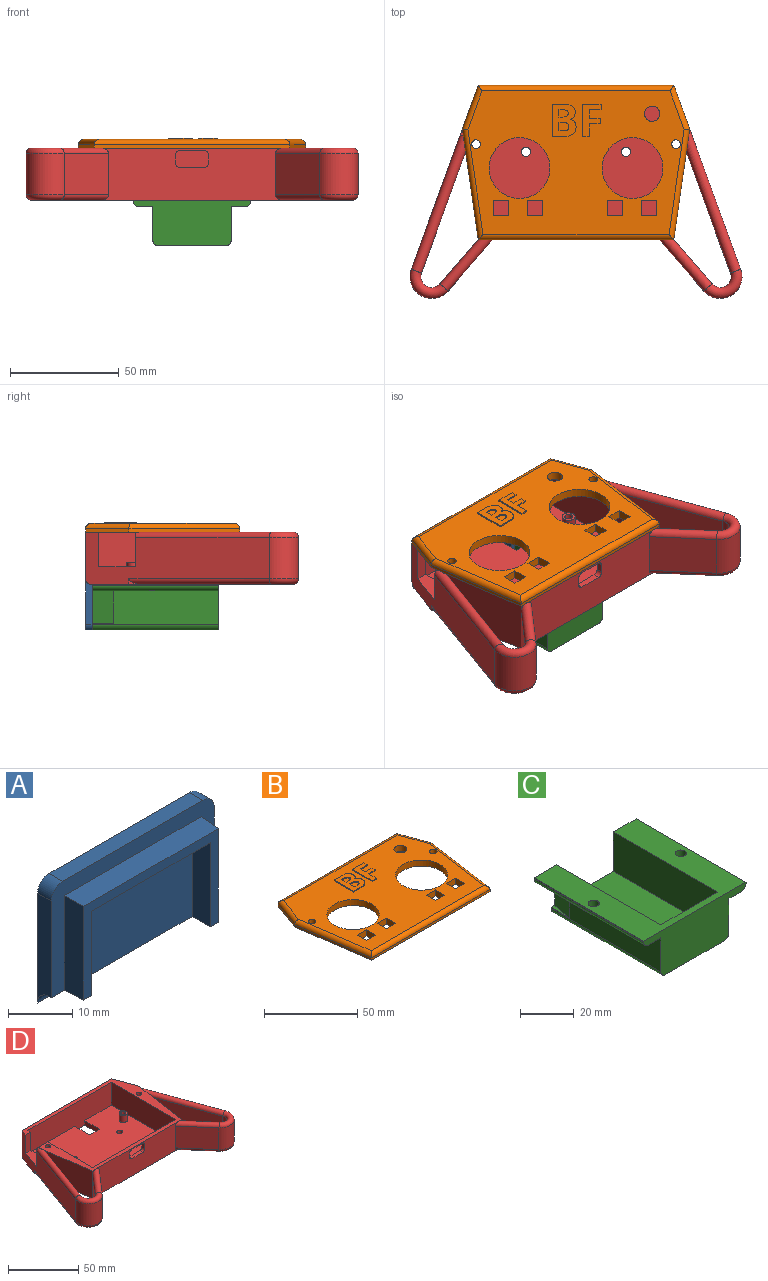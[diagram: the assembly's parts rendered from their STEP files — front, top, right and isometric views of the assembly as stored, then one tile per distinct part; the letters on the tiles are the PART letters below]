
ASSEMBLY  parts=4 mates=7
PART A: 17 faces, bbox 36x7x23.5 mm
  f0: plane 36x21mm, normal (0,-1,0), area 206.7mm2, adj f1,f2,f3,f4,f5,f6,f13,f14
  f1: cylinder r=2.5mm len=3mm, axis (0,1,0), area 11.8mm2, adj f0,f2,f6,f8
  f2: plane 21x3mm, normal (-1,0,0), area 56.8mm2, adj f0,f1,f3,f8,f16
  f3: plane 36x4.5mm, normal (0,0,-1), area 33.2mm2, adj f0,f2,f4,f7,f9,f11,f12,f13
  f4: plane 21x3mm, normal (1,0,0), area 56.8mm2, adj f0,f3,f5,f8,f16
  f5: cylinder r=2.5mm len=3mm, axis (0,1,0), area 11.8mm2, adj f0,f4,f6,f8
  f6: plane 31x3mm, normal (0,0,1), area 93mm2, adj f0,f1,f5,f8
  f7: plane 26.2x16.1mm, normal (0,-1,0), area 421.8mm2, adj f3,f9,f10,f11
  f8: plane 36x23.5mm, normal (0,1,0), area 843.3mm2, adj f1,f2,f4,f5,f6,f16
  f9: plane 16.1x4mm, normal (1,0,0), area 64.4mm2, adj f3,f7,f10,f12
  f10: plane 26.2x4mm, normal (0,0,-1), area 104.8mm2, adj f7,f9,f11,f12
  f11: plane 16.1x4mm, normal (-1,0,0), area 64.4mm2, adj f3,f7,f10,f12
  f12: plane 29.8x17.9mm, normal (0,-1,0), area 111.6mm2, adj f3,f9,f10,f11,f13,f14,f15
  f13: plane 18.1x4mm, normal (-1,-0.05,0), area 72.1mm2, adj f0,f3,f12,f14
  f14: plane 30.2x4mm, normal (0,-0.05,1), area 120.1mm2, adj f0,f12,f13,f15
  f15: plane 18.1x4mm, normal (1,-0.05,0), area 72.1mm2, adj f0,f3,f12,f14
  f16: cylinder r=2.5mm len=36mm, axis (1,0,0), area 141.4mm2, adj f2,f3,f4,f8
PART B: 74 faces, bbox 104.6x71x4.6 mm
  f0: plane 99.43x66mm, normal (0,0,1), area 4401.7mm2, adj f7,f9,f10,f11,f12,f13,f14,f15
  f1: plane 104.56x71mm, normal (0,0,-1), area 5415.7mm2, adj f2,f3,f4,f5,f6,f7,f8,f9
  f2: plane 90x1.5mm, normal (0,1,0), area 135mm2, adj f1,f3,f8,f13
  f3: plane 20x7.28mm, normal (-0.94,0.34,0), area 31.9mm2, adj f1,f2,f4,f11
  f4: plane 51x7.28mm, normal (-0.99,-0.14,0), area 77.3mm2, adj f1,f3,f5,f10
  f5: plane 90x1.5mm, normal (0,-1,0), area 135mm2, adj f1,f4,f6,f12
  f6: plane 51x7.28mm, normal (0.99,-0.14,0), area 77.3mm2, adj f1,f5,f8,f14
  f7: cylinder r=2mm len=4mm, axis (0,0,-1), area 50.3mm2, adj f0,f1
  f8: plane 20x7.28mm, normal (0.94,0.34,0), area 31.9mm2, adj f1,f2,f6,f15
  f9: cylinder r=2mm len=4mm, axis (0,0,-1), area 50.3mm2, adj f0,f1
  f10: cylinder r=2.5mm len=51.35mm, axis (-0.14,0.99,0), area 198.3mm2, adj f0,f4,f11,f12
  f11: cylinder r=2.5mm len=20.86mm, axis (0.34,0.94,0), area 80.2mm2, adj f0,f3,f10,f13
  f12: cylinder r=2.5mm len=90mm, axis (-1,0,0), area 347.2mm2, adj f0,f5,f10,f14
  f13: cylinder r=2.5mm len=90mm, axis (1,0,0), area 348.4mm2, adj f0,f2,f11,f15
  f14: cylinder r=2.5mm len=51.35mm, axis (-0.14,-0.99,0), area 198.3mm2, adj f0,f6,f12,f15
  f15: cylinder r=2.5mm len=20.86mm, axis (0.34,-0.94,0), area 80.2mm2, adj f0,f8,f13,f14
  f16: cylinder r=14mm len=28mm, axis (0,0,1), area 351.9mm2, adj f0,f1
  f17: cylinder r=3.5mm len=7mm, axis (0,0,1), area 88mm2, adj f0,f1
  f18: plane 7x4mm, normal (0,-1,0), area 28mm2, adj f0,f1,f19,f21
  f19: plane 7x4mm, normal (1,0,0), area 28mm2, adj f0,f1,f18,f20
  f20: plane 7x4mm, normal (0,1,0), area 28mm2, adj f0,f1,f19,f21
  f21: plane 7x4mm, normal (-1,0,0), area 28mm2, adj f0,f1,f18,f20
  f22: cylinder r=14mm len=28mm, axis (0,0,1), area 351.9mm2, adj f0,f1
  f23: plane 7x4mm, normal (-1,0,0), area 28mm2, adj f0,f1,f24,f26
  f24: plane 7x4mm, normal (0,-1,0), area 28mm2, adj f0,f1,f23,f25
  f25: plane 7x4mm, normal (1,0,0), area 28mm2, adj f0,f1,f24,f26
  f26: plane 7x4mm, normal (0,1,0), area 28mm2, adj f0,f1,f23,f25
  f27: plane 7x4mm, normal (0,-1,0), area 28mm2, adj f0,f1,f28,f30
  f28: plane 7x4mm, normal (1,0,0), area 28mm2, adj f0,f1,f27,f29
  f29: plane 7x4mm, normal (0,1,0), area 28mm2, adj f0,f1,f28,f30
  f30: plane 7x4mm, normal (-1,0,0), area 28mm2, adj f0,f1,f27,f29
  f31: plane 7x4mm, normal (0,-1,0), area 28mm2, adj f0,f1,f32,f34
  f32: plane 7x4mm, normal (1,0,0), area 28mm2, adj f0,f1,f31,f33
  f33: plane 7x4mm, normal (0,1,0), area 28mm2, adj f0,f1,f32,f34
  f34: plane 7x4mm, normal (-1,0,0), area 28mm2, adj f0,f1,f31,f33
  f35: plane 3.88x0.6mm, normal (1,0,0), area 2.3mm2, adj f36,f59,f60,f62
  f36: plane 1.95x0.6mm, normal (0,-1,0), area 1.2mm2, adj f35,f37,f60,f62
  f37: extruded ~2.64x1.85mm, area 2.2mm2, adj f36,f38,f60,f62
  f38: extruded ~1.53x0.62mm, area 1mm2, adj f37,f39,f60,f62
  f39: extruded ~1.92x0.6mm, area 1.2mm2, adj f38,f59,f60,f62
  f40: plane 1.83x0.6mm, normal (0,1,0), area 1.1mm2, adj f41,f57,f60,f61
  f41: plane 3.31x0.6mm, normal (1,0,0), area 2mm2, adj f40,f42,f60,f61
  f42: plane 1.66x0.6mm, normal (0,-1,0), area 1mm2, adj f41,f43,f60,f61
  f43: extruded ~1.98x0.6mm, area 1.2mm2, adj f42,f44,f60,f61
  f44: extruded ~1.23x0.63mm, area 0.9mm2, adj f43,f45,f60,f61
  f45: extruded ~1.31x0.6mm, area 0.9mm2, adj f44,f57,f60,f61
  f46: plane 4.63x0.6mm, normal (0,1,0), area 2.8mm2, adj f0,f47,f58,f60
  f47: plane 14.87x0.6mm, normal (-1,0,0), area 8.9mm2, adj f0,f46,f48,f60
  f48: plane 5.56x0.6mm, normal (0,-1,0), area 3.3mm2, adj f0,f47,f49,f60
  f49: extruded ~3.99x1.14mm, area 2.5mm2, adj f0,f48,f50,f60
  f50: extruded ~3.17x1.47mm, area 2.2mm2, adj f0,f49,f51,f60
  f51: extruded ~2.3x0.63mm, area 1.5mm2, adj f0,f50,f52,f60
  f52: extruded ~2.04x1.18mm, area 1.4mm2, adj f0,f51,f53,f60
  f53: plane 0.6x0.1mm, normal (1,0,0), area 0.1mm2, adj f0,f52,f54,f60
  f54: extruded ~1.66x1.03mm, area 1.2mm2, adj f0,f53,f55,f60
  f55: extruded ~2.19x0.63mm, area 1.4mm2, adj f0,f54,f56,f60
  f56: extruded ~2.86x1.43mm, area 2mm2, adj f0,f55,f58,f60
  f57: extruded ~1.86x0.6mm, area 1.2mm2, adj f40,f45,f60,f61
  f58: extruded ~4.59x0.9mm, area 2.8mm2, adj f0,f46,f56,f60
  f59: plane 2.05x0.6mm, normal (0,1,0), area 1.2mm2, adj f35,f39,f60,f62
  f60: plane 14.87x11.03mm, normal (0,0,1), area 120.6mm2, adj f35,f36,f37,f38,f39,f40,f41,f42
  f61: plane 4.26x3.31mm, normal (0,0,1), area 12.8mm2, adj f40,f41,f42,f43,f44,f45,f57
  f62: plane 4.6x3.88mm, normal (0,0,1), area 16.2mm2, adj f35,f36,f37,f38,f39,f59
  f63: plane 3.1x0.6mm, normal (0,-1,0), area 1.9mm2, adj f0,f64,f72,f73
  f64: plane 5.88x0.6mm, normal (1,0,0), area 3.5mm2, adj f0,f63,f65,f73
  f65: plane 5.05x0.6mm, normal (0,-1,0), area 3mm2, adj f0,f64,f66,f73
  f66: plane 2.58x0.6mm, normal (1,0,0), area 1.5mm2, adj f0,f65,f67,f73
  f67: plane 5.05x0.6mm, normal (0,1,0), area 3mm2, adj f0,f66,f68,f73
  f68: plane 3.83x0.6mm, normal (1,0,0), area 2.3mm2, adj f0,f67,f69,f73
  f69: plane 5.42x0.6mm, normal (0,-1,0), area 3.3mm2, adj f0,f68,f70,f73
  f70: plane 2.58x0.6mm, normal (1,0,0), area 1.6mm2, adj f0,f69,f71,f73
  f71: plane 8.53x0.6mm, normal (0,1,0), area 5.1mm2, adj f0,f70,f72,f73
  f72: plane 14.87x0.6mm, normal (-1,0,0), area 8.9mm2, adj f0,f63,f71,f73
  f73: plane 14.87x8.53mm, normal (0,0,1), area 73.1mm2, adj f63,f64,f65,f66,f67,f68,f69,f70
PART C: 24 faces, bbox 54x58x21 mm
  f0: plane 54x21mm, normal (0,1,0), area 204.6mm2, adj f1,f2,f3,f4,f5,f6,f7,f8
  f1: plane 58x54mm, normal (0,0,1), area 1454.3mm2, adj f0,f2,f8,f9,f10,f11,f12,f14
  f2: plane 58x0.5mm, normal (-1,0,0), area 29mm2, adj f0,f1,f9,f16
  f3: plane 58x8.5mm, normal (0,0,-1), area 374.4mm2, adj f0,f4,f9,f15,f16,f20
  f4: plane 58x15.5mm, normal (-1,0,0), area 749mm2, adj f0,f3,f9,f17,f20,f21
  f5: plane 58x31mm, normal (0,0,-1), area 1798mm2, adj f0,f9,f17,f18
  f6: plane 58x15.5mm, normal (1,0,0), area 749mm2, adj f0,f7,f9,f18,f22,f23
  f7: plane 58x8.5mm, normal (0,0,-1), area 374.4mm2, adj f0,f6,f9,f14,f19,f22
  f8: plane 58x0.5mm, normal (1,0,0), area 29mm2, adj f0,f1,f9,f19
  f9: plane 54x21mm, normal (0,-1,0), area 804.6mm2, adj f1,f2,f3,f4,f5,f6,f7,f8
  f10: plane 55x18mm, normal (1,0,0), area 990mm2, adj f0,f1,f11,f13
  f11: plane 30x18mm, normal (0,1,0), area 540mm2, adj f1,f10,f12,f13
  f12: plane 55x18mm, normal (-1,0,0), area 990mm2, adj f0,f1,f11,f13
  f13: plane 55x30mm, normal (0,0,1), area 1650mm2, adj f0,f10,f11,f12
  f14: cylinder r=2.1mm len=4.2mm, axis (0,0,1), area 39.5mm2, adj f1,f7,f19
  f15: cylinder r=2.1mm len=4.2mm, axis (0,0,1), area 39.5mm2, adj f1,f3,f16
  f16: cylinder r=2.5mm len=58mm, axis (0,1,0), area 226.5mm2, adj f0,f2,f3,f9,f15
  f17: cylinder r=2.5mm len=58mm, axis (0,1,0), area 227.8mm2, adj f0,f4,f5,f9
  f18: cylinder r=2.5mm len=58mm, axis (0,1,0), area 227.8mm2, adj f0,f5,f6,f9
  f19: cylinder r=2.5mm len=58mm, axis (0,1,0), area 226.5mm2, adj f0,f7,f8,f9,f14
  f20: plane 15x10mm, normal (-0.98,0.2,0), area 153mm2, adj f0,f3,f4,f21
  f21: plane 10x2mm, normal (0,0,1), area 10mm2, adj f0,f4,f20
  f22: plane 15x10mm, normal (0.98,0.2,0), area 153mm2, adj f0,f6,f7,f23
  f23: plane 10x2mm, normal (0,0,1), area 10mm2, adj f0,f6,f22
PART D: 82 faces, bbox 154.4x98.8x24 mm
  f0: plane 104.13x71mm, normal (0,0,1), area 1283.3mm2, adj f1,f2,f3,f7,f9,f11,f12,f13
  f1: plane 84.58x30.78mm, normal (-0.94,0.34,0), area 1533.7mm2, adj f0,f5,f10,f15,f18,f46,f49,f50
  f2: plane 83.38x24mm, normal (0,-1,0), area 1732.7mm2, adj f0,f5,f45,f47,f52,f56,f58,f63
  f3: plane 84x20mm, normal (0,1,0), area 1563.4mm2, adj f0,f4,f20,f21,f71,f72,f73,f74
  f4: plane 84x65mm, normal (0,0,1), area 5169.2mm2, adj f3,f19,f20,f21,f23,f27,f31,f35
  f5: plane 104.56x68.5mm, normal (0,0,-1), area 6448.4mm2, adj f1,f2,f6,f8,f9,f10,f11,f14
  f6: plane 3.31x2.5mm, normal (0,-1,0), area 1.8mm2, adj f5,f9,f58
  f7: plane 3.31x2.5mm, normal (0,-1,0), area 1.8mm2, adj f0,f9,f63
  f8: plane 5.25x2.5mm, normal (0.99,-0.14,0), area 2.8mm2, adj f5,f14,f60
  f9: plane 45.75x24mm, normal (0.99,-0.14,0), area 987.5mm2, adj f0,f5,f6,f7,f53,f55,f60,f61
  f10: plane 5.25x2.5mm, normal (-0.99,-0.14,0), area 2.8mm2, adj f1,f5,f49
  f11: plane 45.75x24mm, normal (-0.99,-0.14,0), area 987.5mm2, adj f0,f5,f12,f17,f42,f44,f49,f50
  f12: plane 3.31x2.5mm, normal (0,-1,0), area 1.8mm2, adj f0,f11,f52
  f13: plane 5.25x2.5mm, normal (0.99,-0.14,0), area 2.8mm2, adj f0,f14,f61
  f14: plane 84.58x30.78mm, normal (0.94,0.34,0), area 1815.1mm2, adj f0,f5,f8,f13,f15,f18,f57,f60
  f15: plane 90x21.5mm, normal (0,1,0), area 1935mm2, adj f0,f1,f14,f18
  f16: plane 2.25x0.32mm, normal (-0.99,-0.14,0), area 0.2mm2, adj f0,f50,f81
  f17: plane 3.31x2.5mm, normal (0,-1,0), area 1.8mm2, adj f5,f11,f47
  f18: cylinder r=2.5mm len=91.82mm, axis (-1,0,0), area 356mm2, adj f1,f5,f14,f15
  f19: plane 84x24mm, normal (0,-1,0), area 1720mm2, adj f0,f4,f5,f20,f21,f66,f67
  f20: plane 65x20mm, normal (1,0,0), area 1028mm2, adj f0,f3,f4,f19,f79,f80,f81
  f21: plane 65x20mm, normal (-1,0,0), area 1300mm2, adj f0,f3,f4,f19
  f22: cylinder r=1.75mm len=6mm, axis (0,0,-1), area 66mm2, adj f24,f25
  f23: cylinder r=3mm len=6mm, axis (0,0,-1), area 113.1mm2, adj f4,f24
  f24: plane 6x6mm, normal (0,0,1), area 18.7mm2, adj f22,f23
  f25: plane 3.5x3.5mm, normal (0,0,1), area 2.6mm2, adj f22,f41
  f26: cylinder r=1.75mm len=6mm, axis (0,0,-1), area 66mm2, adj f28,f29
  f27: cylinder r=3mm len=6mm, axis (0,0,-1), area 113.1mm2, adj f4,f28
  f28: plane 6x6mm, normal (0,0,1), area 18.7mm2, adj f26,f27
  f29: plane 3.5x3.5mm, normal (0,0,1), area 2.6mm2, adj f26,f40
  f30: cylinder r=1.75mm len=6mm, axis (0,0,-1), area 66mm2, adj f32,f33
  f31: cylinder r=3mm len=6mm, axis (0,0,-1), area 113.1mm2, adj f4,f32
  f32: plane 6x6mm, normal (0,0,1), area 18.7mm2, adj f30,f31
  f33: plane 3.5x3.5mm, normal (0,0,1), area 2.6mm2, adj f30,f38
  f34: cylinder r=1.75mm len=6mm, axis (0,0,-1), area 66mm2, adj f36,f37
  f35: cylinder r=3mm len=6mm, axis (0,0,-1), area 113.1mm2, adj f4,f36
  f36: plane 6x6mm, normal (0,0,1), area 18.7mm2, adj f34,f35
  f37: plane 3.5x3.5mm, normal (0,0,1), area 2.6mm2, adj f34,f39
  f38: cylinder r=1.5mm len=4mm, axis (0,0,1), area 37.7mm2, adj f5,f33
  f39: cylinder r=1.5mm len=4mm, axis (0,0,1), area 37.7mm2, adj f5,f37
  f40: cylinder r=1.5mm len=4mm, axis (0,0,1), area 37.7mm2, adj f5,f29
  f41: cylinder r=1.5mm len=4mm, axis (0,0,1), area 37.7mm2, adj f5,f25
  f42: plane 55.79x20.31mm, normal (0.94,-0.34,0), area 1128mm2, adj f11,f43,f49,f50
  f43: cylinder r=5mm len=19mm, axis (0,0,-1), area 263.7mm2, adj f42,f44,f48,f51
  f44: plane 20.28x19mm, normal (-0.75,0.66,0), area 510.3mm2, adj f11,f43,f47,f52
  f45: plane 23.56x20.46mm, normal (0.75,-0.66,0), area 592.8mm2, adj f2,f46,f47,f52
  f46: cylinder r=10mm len=19mm, axis (0,0,-1), area 527.3mm2, adj f1,f45,f48,f51
  f47: cylinder r=2.5mm len=26.84mm, axis (0.66,0.75,0), area 228mm2, adj f2,f17,f44,f45,f48
  f48: torus R=7.5mm, axis (0,0,-1), area 163.5mm2, adj f43,f46,f47,f49
  f49: cylinder r=2.5mm len=66.29mm, axis (-0.34,-0.94,0), area 503mm2, adj f1,f10,f11,f42,f48
  f50: cylinder r=2.5mm len=63.78mm, axis (0.34,0.94,0), area 497.2mm2, adj f1,f11,f16,f42,f51,f81
  f51: torus R=7.5mm, axis (0,0,-1), area 163.5mm2, adj f43,f46,f50,f52
  f52: cylinder r=2.5mm len=26.84mm, axis (-0.66,-0.75,0), area 228mm2, adj f2,f12,f44,f45,f51
  f53: plane 55.79x20.31mm, normal (-0.94,-0.34,0), area 1128mm2, adj f9,f54,f60,f61
  f54: cylinder r=5mm len=19mm, axis (0,0,-1), area 263.7mm2, adj f53,f55,f59,f62
  f55: plane 20.28x19mm, normal (0.75,0.66,0), area 510.3mm2, adj f9,f54,f58,f63
  f56: plane 23.56x20.46mm, normal (-0.75,-0.66,0), area 592.8mm2, adj f2,f57,f58,f63
  f57: cylinder r=10mm len=19mm, axis (0,0,-1), area 527.3mm2, adj f14,f56,f59,f62
  f58: cylinder r=2.5mm len=26.84mm, axis (-0.66,0.75,0), area 228mm2, adj f2,f6,f55,f56,f59
  f59: torus R=7.5mm, axis (0,0,-1), area 163.5mm2, adj f54,f57,f58,f60
  f60: cylinder r=2.5mm len=66.29mm, axis (0.34,-0.94,0), area 503mm2, adj f8,f9,f14,f53,f59
  f61: cylinder r=2.5mm len=66.29mm, axis (-0.34,0.94,0), area 503mm2, adj f9,f13,f14,f53,f62
  f62: torus R=7.5mm, axis (0,0,-1), area 163.5mm2, adj f54,f57,f61,f63
  f63: cylinder r=2.5mm len=26.84mm, axis (0.66,-0.75,0), area 228mm2, adj f2,f7,f55,f56,f62
  f64: cylinder r=2mm len=24mm, axis (0,0,1), area 301.6mm2, adj f0,f5
  f65: cylinder r=2mm len=24mm, axis (0,0,1), area 301.6mm2, adj f0,f5
  f66: plane 15x4mm, normal (-1,0,0), area 60mm2, adj f4,f5,f19,f68
  f67: plane 15x4mm, normal (1,0,0), area 60mm2, adj f4,f5,f19,f68
  f68: plane 10x4mm, normal (0,1,0), area 40mm2, adj f4,f5,f66,f67
  f69: cylinder r=2.1mm len=4.2mm, axis (0,0,1), area 52.8mm2, adj f4,f5
  f70: cylinder r=2.1mm len=4.2mm, axis (0,0,1), area 52.8mm2, adj f4,f5
  f71: plane 4x3mm, normal (-1,0,0), area 12mm2, adj f2,f3,f72,f78
  f72: cylinder r=2mm len=3mm, axis (0,-1,0), area 9.4mm2, adj f2,f3,f71,f73
  f73: plane 11x3mm, normal (0,0,-1), area 33mm2, adj f2,f3,f72,f74
  f74: cylinder r=2mm len=3mm, axis (0,-1,0), area 9.4mm2, adj f2,f3,f73,f75
  f75: plane 4x3mm, normal (1,0,0), area 12mm2, adj f2,f3,f74,f76
  f76: cylinder r=2mm len=3mm, axis (0,-1,0), area 9.4mm2, adj f2,f3,f75,f77
  f77: plane 11x3mm, normal (0,0,1), area 33mm2, adj f2,f3,f76,f78
  f78: cylinder r=2mm len=3mm, axis (0,-1,0), area 9.4mm2, adj f2,f3,f71,f77
  f79: plane 16x5.18mm, normal (0,-1,0), area 82.9mm2, adj f0,f1,f20,f80
  f80: plane 17x11.37mm, normal (0,0,1), area 140.7mm2, adj f1,f20,f79,f81
  f81: plane 16x11.37mm, normal (0,1,0), area 180.6mm2, adj f0,f1,f16,f20,f50,f80
PLACE A rot(axis=(0,1,0),180deg) t=(29.97,64.83,-10.65)mm
PLACE B t=(29.97,29.33,23.85)mm
PLACE C t=(29.97,32.83,-0.15)mm
PLACE D t=(29.97,29.33,-0.15)mm
MATE planar A.f0 <-> C.f0  axis (0,-1,0) through (14.87,61.83,-9.2)mm
MATE planar C.f5 <-> A.f6  axis (0,0,-1) through (29.97,32.83,-21.15)mm
MATE slider B.f7 <-> D.f65  axis (0,0,1) through (-16.03,37.83,27.85)mm
MATE slider C.f14 <-> D.f69  axis (0,0,1) through (52.97,34.33,-3.15)mm
MATE planar D.f0 <-> B.f1  axis (0,0,1) through (34.95,29.08,23.85)mm
MATE planar C.f4 <-> A.f4  axis (-1,0,0) through (11.97,28.02,-10.95)mm
MATE planar D.f30 <-> C.f1  axis (0,0,-1) through (-0.03,1.83,-0.15)mm
